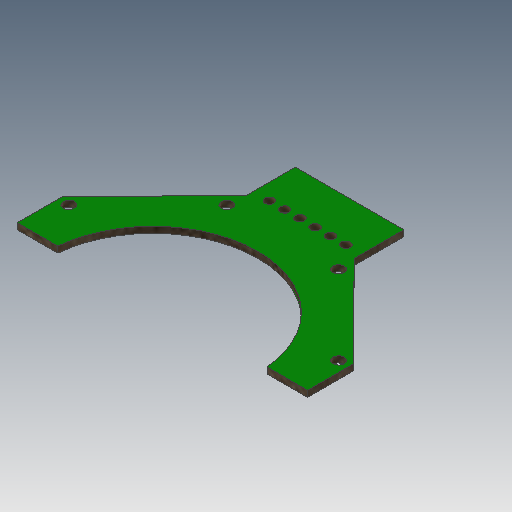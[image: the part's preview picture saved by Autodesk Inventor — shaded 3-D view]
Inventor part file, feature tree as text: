
AUTODESK INVENTOR PART (.ipt)
format: ipt  version: 2020.2 (Build 242310000, 310)  size: 137,216 bytes
history: native  units: mm
features: reference x4, sketch x3, extrude x2, other x2, mirror x1, hole x1, pattern_linear x1
ambient origin geometry x8: Origin, YZ Plane, XZ Plane, XY Plane, X Axis, Y Axis, Z Axis, Center Point
bodies: Body1 (feature_tree)
feature tree (14):
  extrude  "Extrusion7"  Depth=38.0mm
  mirror  "Mirror5"
  hole  "Hole5"  [1 undecoded]
  pattern_linear  "Rectangular Pattern1"  Spacing1=6.5mm  [1 undecoded]
  extrude  "Extrusion8"  Depth=24.5mm
  sketch  "Sketch11"  dims[d82=38.0mm d83=27.5mm]
  sketch  "Sketch12"  dims[d84=14.2mm d85=6.0mm]
  sketch  "Sketch13"  dims[d86=12.0mm d87=6.5mm d88=24.5mm d89=0.8mm d90=0.0mm d91=5.5mm d92=1.0mm d93=1.2mm d94=6.0mm d95=6.3mm d96=2.0mm d97=90.0deg d98=8.0mm d99=20.594885mm d100=60.0mm d102=2.0mm d103=0.0mm d104=0.0mm]
  reference  "Reference1"
  reference  "Reference2"
  reference  "Reference3"
  reference  "Reference4"
  other  "Nema 17 Stepper Motor.iam"
  other  "Nema 17 plastic:1"
note: 2 required parameter values undecoded (feature->parameter linkage not recoverable at this tier; creation-order binding heuristic only, values carry confidence <= 0.55)
